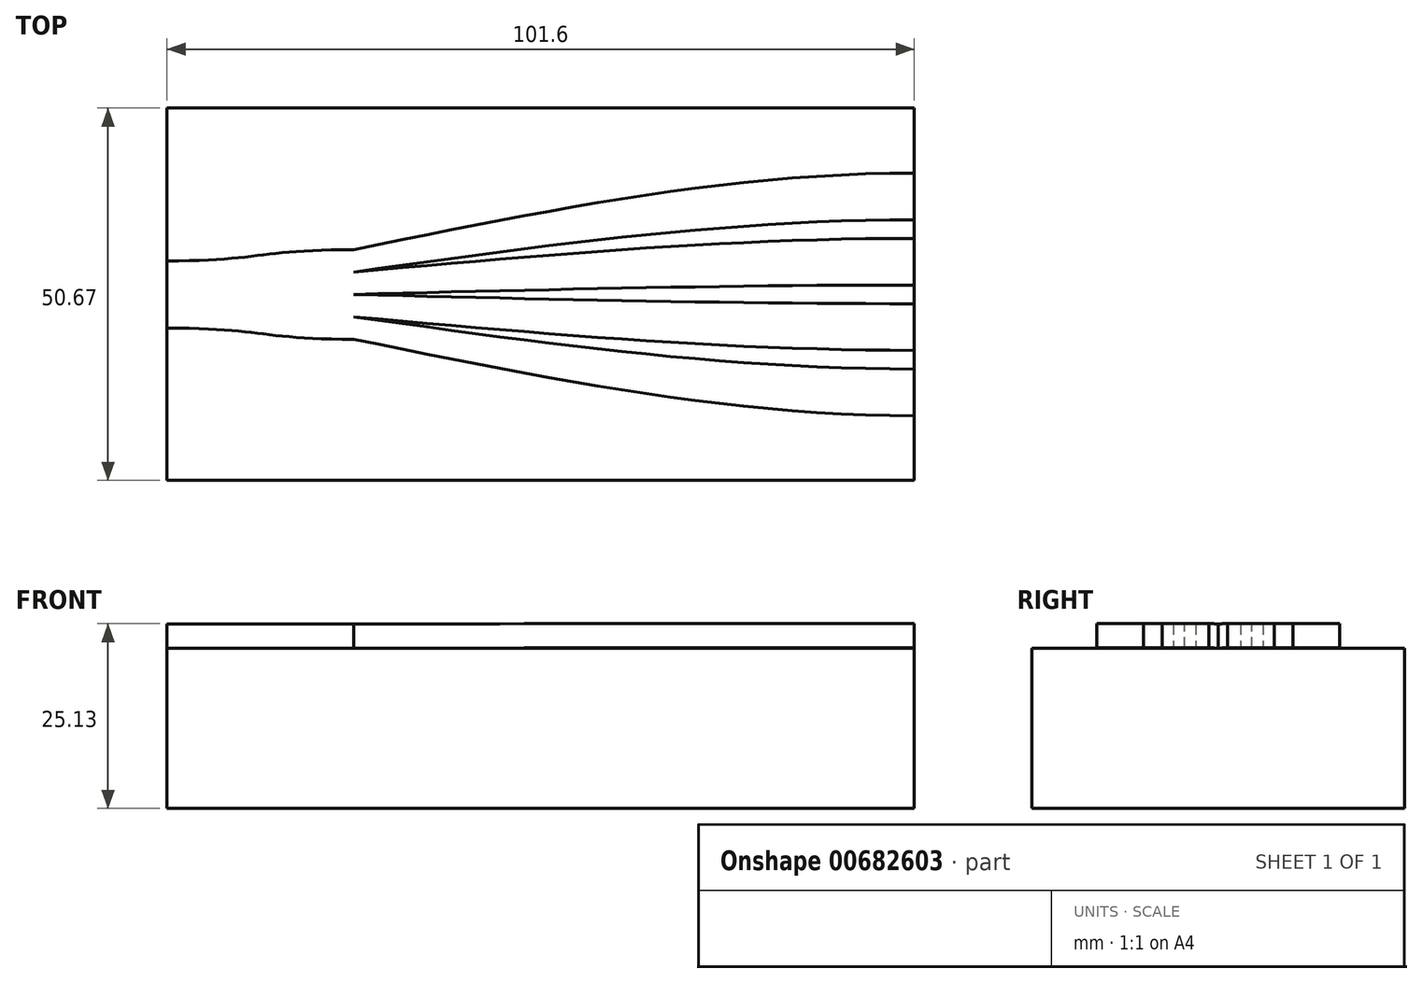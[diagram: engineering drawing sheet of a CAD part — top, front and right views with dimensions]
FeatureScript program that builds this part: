
annotation { "Feature Type Name" : "Feature", "Feature Type Description" : "" }
export const myFeature = defineFeature(function(context is Context, id is Id, definition is map)
    precondition{}
    {
        {
            var Q0;
            Q0=qCreatedBy(makeId("Right.planeOp"),FACE);
            var sketch = newSketch(context, id + "F0", { "sketchPlane" : qUnion([Q0])});
            skLineSegment(sketch, "E0.bottom", {"start": v(-25.3, 21.78) * mm, "end": v(25.37, 21.78) * mm});
            skLineSegment(sketch, "E0.top", {"start": v(-25.3, 0) * mm, "end": v(25.37, 0) * mm});
            skLineSegment(sketch, "E0.left", {"start": v(-25.3, 21.78) * mm, "end": v(-25.3, 0) * mm});
            skLineSegment(sketch, "E0.right", {"start": v(25.37, 21.78) * mm, "end": v(25.37, 0) * mm});
            skSolve(sketch);
        }
        {
            var Q0;
            Q0 = qSketchRegion(id + "F0", true);
            extrude(context, id + "F1", {"entities" : qUnion([Q0]), "depth" : 101.6 * mm, "offsetDistance" : 25.4 * mm});
        }
        {
            var Q0;
            Q0=qCreatedBy(makeId("Right.planeOp"),FACE);
            var sketch = newSketch(context, id + "F2", { "sketchPlane" : qUnion([Q0])});
            skLineSegment(sketch, "E1.bottom", {"start": v(-4.57, 21.8) * mm, "end": v(4.57, 21.8) * mm});
            skLineSegment(sketch, "E1.top", {"start": v(-4.57, 25.1) * mm, "end": v(4.57, 25.1) * mm});
            skLineSegment(sketch, "E1.left", {"start": v(-4.57, 21.8) * mm, "end": v(-4.57, 25.1) * mm});
            skLineSegment(sketch, "E1.right", {"start": v(4.57, 21.8) * mm, "end": v(4.57, 25.1) * mm});
            skPoint(sketch, "E1.middle", {"position": v(0, 23.44) * mm});
            skSolve(sketch);
        }
        {
            var Q0;
            Q0=qCreatedBy(makeId("Right.planeOp"),FACE);
            cPlane(context, id + "F3", {"entities" : qUnion([Q0]), "cplaneType" : CPlaneType.OFFSET, "offset" : 25.4 * mm, "width" : 152.4 * mm, "height" : 152.4 * mm});
        }
        {
            var Q0;
            Q0=qCreatedBy(id+"F3.planeOp",FACE);
            var sketch = newSketch(context, id + "F4", { "sketchPlane" : qUnion([Q0])});
            skLineSegment(sketch, "E2.bottom", {"start": v(-6.1, 25.1) * mm, "end": v(6.1, 25.1) * mm});
            skLineSegment(sketch, "E2.top", {"start": v(-6.1, 21.8) * mm, "end": v(6.1, 21.8) * mm});
            skLineSegment(sketch, "E2.left", {"start": v(-6.1, 25.1) * mm, "end": v(-6.1, 21.8) * mm});
            skLineSegment(sketch, "E2.right", {"start": v(6.1, 25.1) * mm, "end": v(6.1, 21.8) * mm});
            skPoint(sketch, "E2.middle", {"position": v(0, 23.45) * mm});
            skSolve(sketch);
        }
        {
            var Q0;
            Q0 = qSketchRegion(id + "F2", true);
            var Q1;
            Q1 = qSketchRegion(id + "F4", true);
            loft(context, id + "F5", {"startCondition" : LoftEndDerivativeType.NORMAL_TO_PROFILE, "startMagnitude" : 1.5, "endCondition" : LoftEndDerivativeType.NORMAL_TO_PROFILE, "endMagnitude" : 1.5, "sheetProfilesArray" : [{ "sheetProfileEntities" : qUnion([Q0]) }, { "sheetProfileEntities" : qUnion([Q1]) }]});
        }
        {
            var Q0;
            Q0=makeQuery(id+"F5.opLoft","CAP_FACE",FACE,{"disambiguationData":[OSD([makeQuery(id+"F4.imprint","IMPRINT",FACE,{"disambiguationData":[TD([[makeQuery(id+"F4.imprint","IMPRINT",EDGE,{"derivedFrom":sQuery(id+"F4.wireOp",EDGE,"E2.bottom")}),-1.0]])]})])],"isStart":true});
            var sketch = newSketch(context, id + "F6", { "sketchPlane" : qUnion([Q0])});
            skLineSegment(sketch, "E3.bottom", {"start": v(-6.1, 25.1) * mm, "end": v(-3.05, 25.1) * mm});
            skLineSegment(sketch, "E3.top", {"start": v(-6.1, 21.8) * mm, "end": v(-3.05, 21.8) * mm});
            skLineSegment(sketch, "E3.left", {"start": v(-6.1, 25.1) * mm, "end": v(-6.1, 21.8) * mm});
            skLineSegment(sketch, "E3.right", {"start": v(-3.05, 25.1) * mm, "end": v(-3.05, 21.8) * mm});
            skLineSegment(sketch, "E4.bottom", {"start": v(-3.05, 25.1) * mm, "end": v(0, 25.1) * mm});
            skLineSegment(sketch, "E4.top", {"start": v(-3.05, 21.8) * mm, "end": v(0, 21.8) * mm});
            skLineSegment(sketch, "E4.right", {"start": v(0, 25.1) * mm, "end": v(0, 21.8) * mm});
            skLineSegment(sketch, "E5.bottom", {"start": v(0, 25.1) * mm, "end": v(3.05, 25.1) * mm});
            skLineSegment(sketch, "E5.top", {"start": v(0, 21.8) * mm, "end": v(3.05, 21.8) * mm});
            skLineSegment(sketch, "E5.right", {"start": v(3.05, 25.1) * mm, "end": v(3.05, 21.8) * mm});
            skLineSegment(sketch, "E6.bottom", {"start": v(3.05, 25.1) * mm, "end": v(6.1, 25.1) * mm});
            skLineSegment(sketch, "E6.top", {"start": v(3.05, 21.8) * mm, "end": v(6.1, 21.8) * mm});
            skLineSegment(sketch, "E6.right", {"start": v(6.1, 25.1) * mm, "end": v(6.1, 21.8) * mm});
            skSolve(sketch);
        }
        {
            var Q0;
            Q0=makeQuery(id+"F1.opExtrude","CAP_FACE",FACE,{"disambiguationData":[OSD([sQuery(id+"F0.wireOp",EDGE,"E0.bottom"),sQuery(id+"F0.wireOp",EDGE,"E0.top"),sQuery(id+"F0.wireOp",EDGE,"E0.left"),sQuery(id+"F0.wireOp",EDGE,"E0.right")])],"isStart":false});
            cPlane(context, id + "F7", {"entities" : qUnion([Q0]), "cplaneType" : CPlaneType.OFFSET, "offset" : 0 * mm, "width" : 152.4 * mm, "height" : 152.4 * mm});
        }
        {
            var Q0;
            Q0=qCreatedBy(id+"F7.planeOp",FACE);
            var sketch = newSketch(context, id + "F8", { "sketchPlane" : qUnion([Q0])});
            skLineSegment(sketch, "E7.bottom", {"start": v(-16.5, 25.13) * mm, "end": v(-10.16, 25.13) * mm});
            skLineSegment(sketch, "E7.top", {"start": v(-16.5, 21.82) * mm, "end": v(-10.16, 21.82) * mm});
            skLineSegment(sketch, "E7.left", {"start": v(-16.5, 25.13) * mm, "end": v(-16.5, 21.82) * mm});
            skLineSegment(sketch, "E7.right", {"start": v(-10.16, 25.13) * mm, "end": v(-10.16, 21.82) * mm});
            skLineSegment(sketch, "E8.1.0.0", {"start": v(-7.61, 25.13) * mm, "end": v(-7.61, 21.82) * mm});
            skLineSegment(sketch, "E8.1.0.1", {"start": v(-7.61, 25.13) * mm, "end": v(-1.27, 25.13) * mm});
            skLineSegment(sketch, "E8.1.0.2", {"start": v(-1.27, 25.13) * mm, "end": v(-1.27, 21.82) * mm});
            skLineSegment(sketch, "E8.1.0.3", {"start": v(-7.61, 21.82) * mm, "end": v(-1.27, 21.82) * mm});
            skLineSegment(sketch, "E8.2.0.0", {"start": v(1.28, 25.13) * mm, "end": v(1.28, 21.82) * mm});
            skLineSegment(sketch, "E8.2.0.1", {"start": v(1.28, 25.13) * mm, "end": v(7.62, 25.13) * mm});
            skLineSegment(sketch, "E8.2.0.2", {"start": v(7.62, 25.13) * mm, "end": v(7.62, 21.82) * mm});
            skLineSegment(sketch, "E8.2.0.3", {"start": v(1.28, 21.82) * mm, "end": v(7.62, 21.82) * mm});
            skLineSegment(sketch, "E8.3.0.0", {"start": v(10.17, 25.13) * mm, "end": v(10.17, 21.82) * mm});
            skLineSegment(sketch, "E8.3.0.1", {"start": v(10.17, 25.13) * mm, "end": v(16.51, 25.13) * mm});
            skLineSegment(sketch, "E8.3.0.2", {"start": v(16.51, 25.13) * mm, "end": v(16.51, 21.82) * mm});
            skLineSegment(sketch, "E8.3.0.3", {"start": v(10.17, 21.82) * mm, "end": v(16.51, 21.82) * mm});
            skLineSegment(sketch, "E8.direction1", {"start": v(-16.5, 21.82) * mm, "end": v(-7.61, 21.82) * mm, "construction": true});
            skSolve(sketch);
        }
        {
            var Q1;
            Q1=makeQuery(id+"F6.imprint","IMPRINT",FACE,{"disambiguationData":[TD([[makeQuery(id+"F6.imprint","IMPRINT",EDGE,{"derivedFrom":sQuery(id+"F6.wireOp",EDGE,"E3.bottom")}),1.0]])]});
            var Q2;
            Q2=makeQuery(id+"F8.imprint","IMPRINT",FACE,{"disambiguationData":[TD([[makeQuery(id+"F8.imprint","IMPRINT",EDGE,{"derivedFrom":sQuery(id+"F8.wireOp",EDGE,"E7.bottom")}),-1.0]])]});
            var Q3;
            Q3=sQuery(id+"F6.wireOp",VERTEX,"E3.right.start");
            var Q4;
            Q4=sQuery(id+"F6.wireOp",VERTEX,"E3.left.end");
            loft(context, id + "F9", {"operationType" : NewBodyOperationType.ADD, "endCondition" : LoftEndDerivativeType.NORMAL_TO_PROFILE, "endMagnitude" : 1, "sheetProfilesArray" : [{ "sheetProfileEntities" : qUnion([Q1]) }, { "sheetProfileEntities" : qUnion([Q2]) }], "connections" : [{ "connectionEntities" : qUnion([Q3, Q4]), "connectionEdgeQueries" : qUnion([]), "connectionEdgeParameters" : [] }]});
        }
        {
            var Q1;
            Q1=makeQuery(id+"F6.imprint","IMPRINT",FACE,{"disambiguationData":[TD([[makeQuery(id+"F6.imprint","IMPRINT",EDGE,{"derivedFrom":sQuery(id+"F6.wireOp",EDGE,"E4.bottom")}),1.0]])]});
            var Q2;
            Q2=makeQuery(id+"F8.imprint","IMPRINT",FACE,{"disambiguationData":[TD([[makeQuery(id+"F8.imprint","IMPRINT",EDGE,{"derivedFrom":sQuery(id+"F8.wireOp",EDGE,"E8.1.0.0")}),1.0]])]});
            loft(context, id + "F10", {"operationType" : NewBodyOperationType.ADD, "endCondition" : LoftEndDerivativeType.NORMAL_TO_PROFILE, "endMagnitude" : 1, "sheetProfilesArray" : [{ "sheetProfileEntities" : qUnion([Q1]) }, { "sheetProfileEntities" : qUnion([Q2]) }]});
        }
        {
            var Q1;
            Q1=makeQuery(id+"F6.imprint","IMPRINT",FACE,{"disambiguationData":[TD([[makeQuery(id+"F6.imprint","IMPRINT",EDGE,{"derivedFrom":sQuery(id+"F6.wireOp",EDGE,"E5.bottom")}),1.0]])]});
            var Q2;
            Q2=makeQuery(id+"F8.imprint","IMPRINT",FACE,{"disambiguationData":[TD([[makeQuery(id+"F8.imprint","IMPRINT",EDGE,{"derivedFrom":sQuery(id+"F8.wireOp",EDGE,"E8.2.0.0")}),1.0]])]});
            loft(context, id + "F11", {"operationType" : NewBodyOperationType.ADD, "endCondition" : LoftEndDerivativeType.NORMAL_TO_PROFILE, "endMagnitude" : 1, "sheetProfilesArray" : [{ "sheetProfileEntities" : qUnion([Q1]) }, { "sheetProfileEntities" : qUnion([Q2]) }]});
        }
        {
            var Q1;
            Q1=makeQuery(id+"F6.imprint","IMPRINT",FACE,{"disambiguationData":[TD([[makeQuery(id+"F6.imprint","IMPRINT",EDGE,{"derivedFrom":sQuery(id+"F6.wireOp",EDGE,"E6.bottom")}),1.0]])]});
            var Q2;
            Q2=makeQuery(id+"F8.imprint","IMPRINT",FACE,{"disambiguationData":[TD([[makeQuery(id+"F8.imprint","IMPRINT",EDGE,{"derivedFrom":sQuery(id+"F8.wireOp",EDGE,"E8.3.0.0")}),1.0]])]});
            loft(context, id + "F12", {"operationType" : NewBodyOperationType.ADD, "endCondition" : LoftEndDerivativeType.NORMAL_TO_PROFILE, "endMagnitude" : 1, "sheetProfilesArray" : [{ "sheetProfileEntities" : qUnion([Q1]) }, { "sheetProfileEntities" : qUnion([Q2]) }]});
        }
    });
